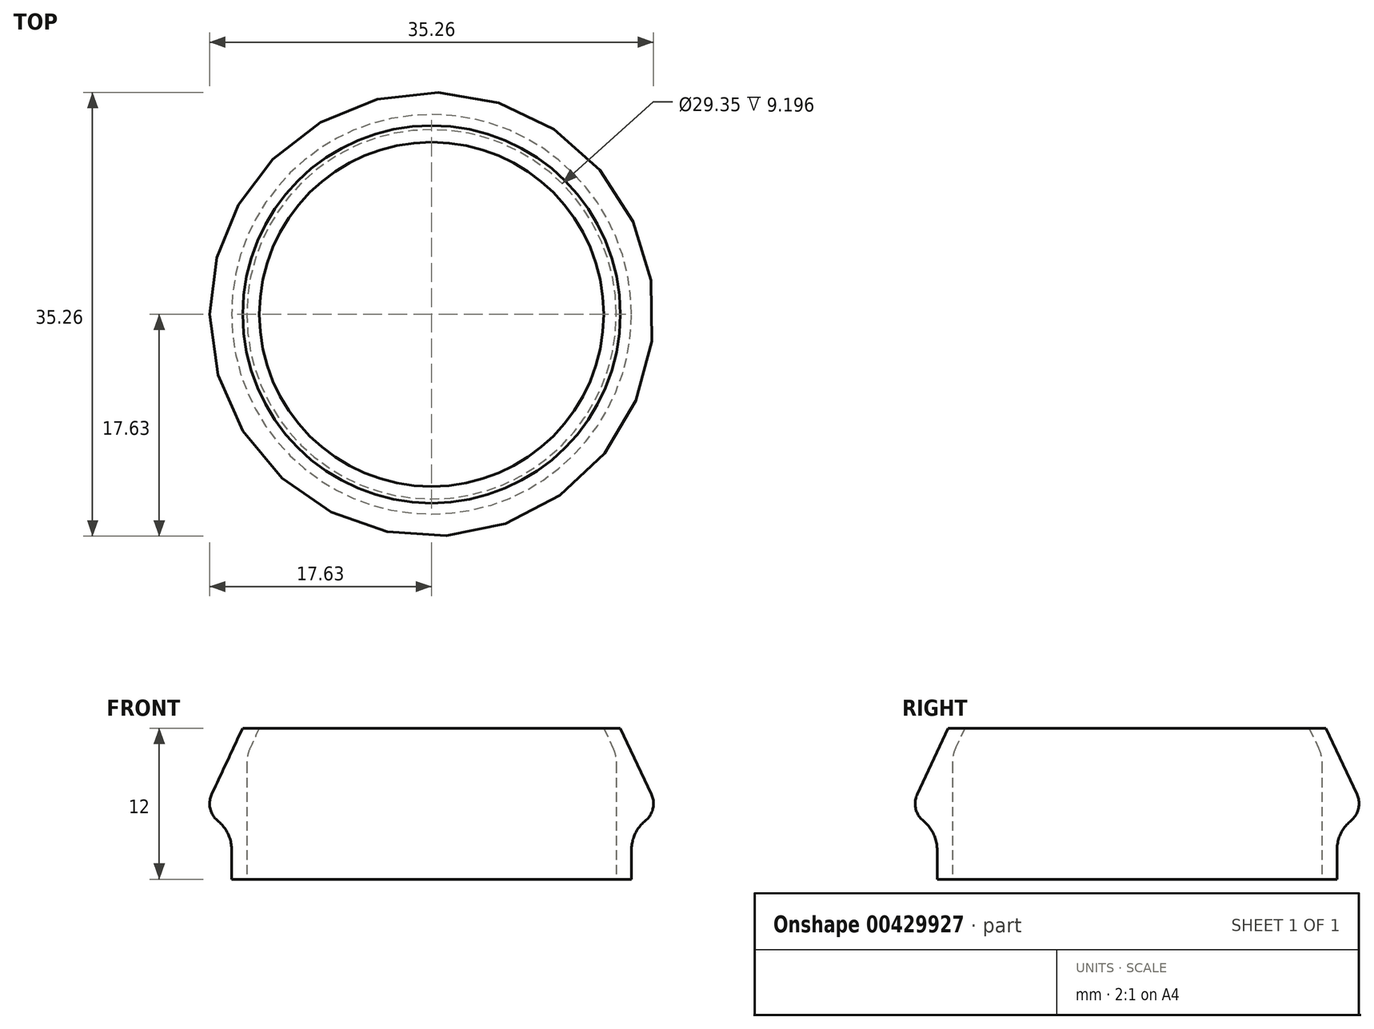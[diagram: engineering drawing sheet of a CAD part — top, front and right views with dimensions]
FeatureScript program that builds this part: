
annotation { "Feature Type Name" : "Feature", "Feature Type Description" : "" }
export const myFeature = defineFeature(function(context is Context, id is Id, definition is map)
    precondition{}
    {
        {
            var Q0;
            Q0=qCreatedBy(makeId("Front.planeOp"),FACE);
            var sketch = newSketch(context, id + "F0", { "sketchPlane" : qUnion([Q0])});
            skLineSegment(sketch, "E0", {"start": v(15, 6) * mm, "end": v(17.46, 0.74) * mm});
            skArc(sketch, "E1", {"start": v(15.88, -1.75) * mm, "mid": v(17.62, 0) * mm, "end": v(15.88, 1.75) * mm});
            skLineSegment(sketch, "E2", {"start": v(15.88, 1.75) * mm, "end": v(15.88, 0) * mm});
            skLineSegment(sketch, "E3", {"start": v(15.88, 0) * mm, "end": v(15.88, -1.75) * mm});
            skLineSegment(sketch, "E4", {"start": v(13.68, 6) * mm, "end": v(15.67, 1.74) * mm});
            skLineSegment(sketch, "E5", {"start": v(15, 6) * mm, "end": v(13.68, 6) * mm});
            skLineSegment(sketch, "E6", {"start": v(15.88, -1.75) * mm, "end": v(15.88, -6) * mm});
            skLineSegment(sketch, "E7", {"start": v(14.67, -6) * mm, "end": v(14.67, 3.86) * mm});
            skLineSegment(sketch, "E8", {"start": v(15.88, -6) * mm, "end": v(14.67, -6) * mm});
            skSolve(sketch);
        }
        {
            var Q0;
            Q0=qCreatedBy(makeId("Front.planeOp"),FACE);
            var sketch = newSketch(context, id + "F1", { "sketchPlane" : qUnion([Q0])});
            skLineSegment(sketch, "E9.0", {"start": v(14.67, -6) * mm, "end": v(14.67, 3.2) * mm});
            skLineSegment(sketch, "E9.1", {"start": v(13.68, 6) * mm, "end": v(14.4, 4.47) * mm});
            skLineSegment(sketch, "E9.2", {"start": v(15, 6) * mm, "end": v(13.68, 6) * mm});
            skLineSegment(sketch, "E9.3", {"start": v(15, 6) * mm, "end": v(17.46, 0.74) * mm});
            skArc(sketch, "E9.4", {"start": v(16.98, -1.36) * mm, "mid": v(17.58, -0.4) * mm, "end": v(17.46, 0.74) * mm});
            skLineSegment(sketch, "E9.5", {"start": v(15.88, -3.68) * mm, "end": v(15.88, -6) * mm});
            skLineSegment(sketch, "E9.6", {"start": v(15.88, -6) * mm, "end": v(14.67, -6) * mm});
            skPoint(sketch, "E10.orphan", {"position": v(15.67, 1.74) * mm});
            skPoint(sketch, "E11.orphan", {"position": v(15.88, 1.75) * mm});
            skPoint(sketch, "E12.visualSharp", {"position": v(14.67, 3.86) * mm});
            skArc(sketch, "E12.filletArc", {"start": v(14.67, 3.2) * mm, "mid": v(14.6, 3.85) * mm, "end": v(14.4, 4.47) * mm});
            skPoint(sketch, "E13.visualSharp", {"position": v(15.88, -1.75) * mm});
            skArc(sketch, "E13.filletArc", {"start": v(16.98, -1.36) * mm, "mid": v(16.17, -2.4) * mm, "end": v(15.88, -3.68) * mm});
            skLineSegment(sketch, "E14", {"start": v(0, 0) * mm, "end": v(0, 26.81) * mm, "construction": true});
            skSolve(sketch);
        }
        {
            var Q0;
            Q0=makeQuery(id+"F1.imprint","IMPRINT",FACE,{"disambiguationData":[TD([[makeQuery(id+"F1.imprint","IMPRINT",EDGE,{"derivedFrom":sQuery(id+"F1.wireOp",EDGE,"E9.0")}),-1.0]])]});
            var Q1;
            Q1=sQuery(id+"F1.wireOp",EDGE,"E14");
            revolve(context, id + "F2", {"entities" : qUnion([Q0]), "axis" : qUnion([Q1]), "revolveType" : RevolveType.FULL});
        }
    });
